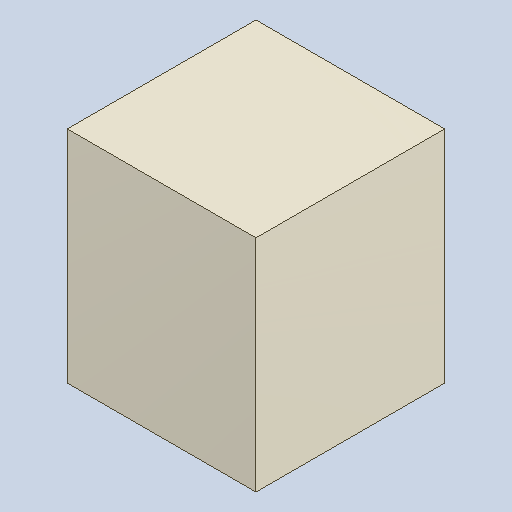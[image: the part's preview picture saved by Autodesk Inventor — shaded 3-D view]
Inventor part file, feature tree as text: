
AUTODESK INVENTOR PART (.ipt)
format: ipt  version: 2023.4 (Build 274418000, 418)  size: 82,944 bytes
history: native  units: mm
features: extrude x1
ambient origin geometry x8: Origin, YZ Plane, XZ Plane, XY Plane, X Axis, Y Axis, Z Axis, Center Point
bodies: Solid1 (feature_tree)
feature tree (1):
  extrude  "Extruded_3"  [1 undecoded]
note: 1 required parameter value undecoded (feature->parameter linkage not recoverable at this tier; creation-order binding heuristic only, values carry confidence <= 0.55)
